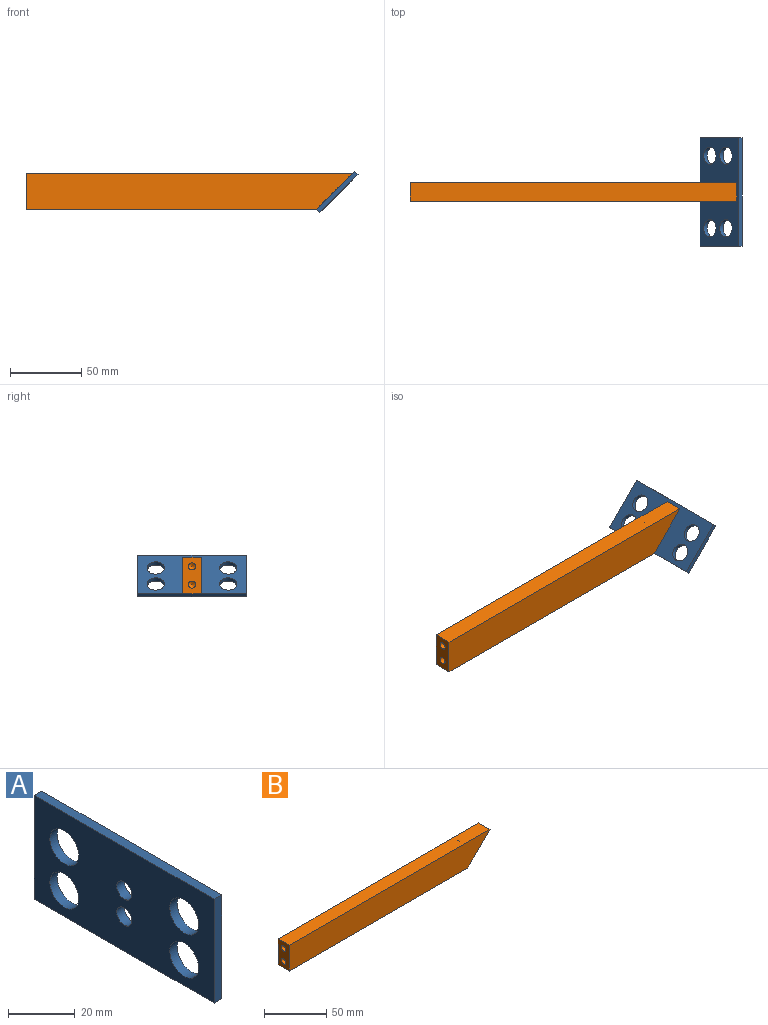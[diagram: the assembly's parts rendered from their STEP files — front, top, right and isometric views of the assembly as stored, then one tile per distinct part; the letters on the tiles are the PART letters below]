
ASSEMBLY  parts=2 mates=1
PART A: 12 faces, bbox 3.2x76.2x38.1 mm
  f0: plane 38.1x3.18mm, normal (0,-1,0), area 121mm2, adj f1,f3,f4,f5
  f1: plane 76.2x3.18mm, normal (0,0,-1), area 241.9mm2, adj f0,f2,f4,f5
  f2: plane 38.1x3.18mm, normal (0,1,0), area 121mm2, adj f1,f3,f4,f5
  f3: plane 76.2x3.18mm, normal (0,0,1), area 241.9mm2, adj f0,f2,f4,f5
  f4: plane 76.2x38.1mm, normal (1,0,0), area 2372.9mm2, adj f0,f1,f2,f3,f6,f7,f8,f9
  f5: plane 76.2x38.1mm, normal (-1,0,0), area 2372.9mm2, adj f0,f1,f2,f3,f6,f7,f8,f9
  f6: cylinder r=3.17mm len=6.35mm, axis (1,0,0), area 63.3mm2, adj f4,f5
  f7: cylinder r=3.17mm len=6.35mm, axis (1,0,0), area 63.3mm2, adj f4,f5
  f8: cylinder r=6.1mm len=12.19mm, axis (1,0,0), area 121.6mm2, adj f4,f5
  f9: cylinder r=6.1mm len=12.19mm, axis (1,0,0), area 121.6mm2, adj f4,f5
  f10: cylinder r=6.1mm len=12.19mm, axis (1,0,0), area 121.6mm2, adj f4,f5
  f11: cylinder r=6.1mm len=12.19mm, axis (1,0,0), area 121.6mm2, adj f4,f5
PART B: 12 faces, bbox 228.6x12.7x25.4 mm
  f0: plane 228.6x12.7mm, normal (0,0,1), area 2903.2mm2, adj f1,f3,f4,f5
  f1: plane 25.4x12.7mm, normal (-1,0,0), area 284mm2, adj f0,f2,f4,f5,f7,f9
  f2: plane 203.2x12.7mm, normal (0,0,-1), area 2580.6mm2, adj f1,f3,f4,f5
  f3: plane 25.4x25.4mm, normal (0.71,0,-0.71), area 436.9mm2, adj f0,f2,f4,f5,f11
  f4: plane 228.6x25.4mm, normal (0,-1,0), area 5483.9mm2, adj f0,f1,f2,f3
  f5: plane 228.6x25.4mm, normal (0,1,0), area 5483.9mm2, adj f0,f1,f2,f3
  f6: cone r=0mm half-angle=59deg, axis (-1,0,0), area 22.5mm2, adj f7
  f7: cylinder r=2.48mm len=25.4mm, axis (-1,0,0), area 395.2mm2, adj f1,f6
  f8: cone r=0mm half-angle=59deg, axis (-1,0,0), area 22.5mm2, adj f9
  f9: cylinder r=2.48mm len=25.4mm, axis (-1,0,0), area 395.2mm2, adj f1,f8
  f10: cone r=0mm half-angle=59deg, axis (0.71,0,-0.71), area 22.5mm2, adj f11
  f11: cylinder r=2.48mm len=17.87mm, axis (0.71,0,-0.71), area 316.2mm2, adj f3,f10
PLACE A rot(axis=(0,1,0),45deg) t=(132.03,-17.53,18.91)mm
PLACE B t=(-71.17,26.92,18.91)mm
MATE fastened A.f6 <-> B.f10  axis (-0.71,0,0.71) through (141.01,20.57,27.89)mm
